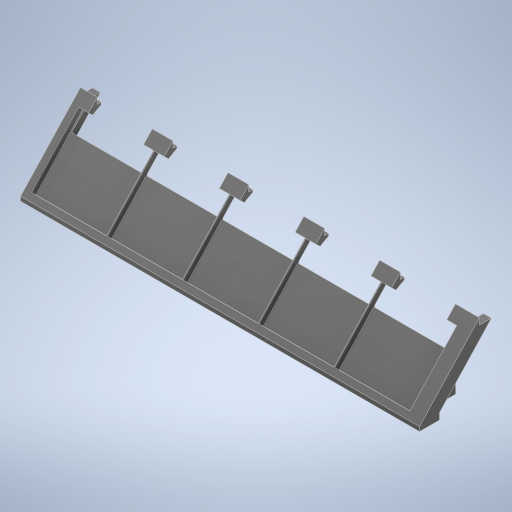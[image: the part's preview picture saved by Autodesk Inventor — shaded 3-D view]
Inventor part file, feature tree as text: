
AUTODESK INVENTOR PART (.ipt)
format: ipt  version: 2023 (Build 270158000, 158)  size: 503,808 bytes
history: native  units: mm
features: extrude x9, sketch x9, projected_geometry x8, plane x3, mirror x2, pattern_linear x1, chamfer x1
ambient origin geometry x8: Origin, YZ Plane, XZ Plane, XY Plane, X Axis, Y Axis, Z Axis, Center Point
bodies: Solid1 (feature_tree)
feature tree (33):
  extrude  "Extrusion1"  Depth=1.6mm
  plane  "Work Plane1"
  extrude  "Extrusion2"  Depth=4.0mm
  extrude  "Extrusion3"  Depth=3.0mm
  plane  "Work Plane2"
  mirror  "Mirror1"
  pattern_linear  "Rectangular Pattern1"  Count1=10 Spacing1=0.0mm
  extrude  "Extrusion4"  [1 undecoded]
  extrude  "Extrusion5"  Depth=3.0mm
  extrude  "Extrusion6"  Depth=3.0mm
  chamfer  "Chamfer1"  Distance=18.8mm
  extrude  "Extrusion7"  Depth=2.5mm TaperAngle=0.0deg
  extrude  "Extrusion8"  Depth=8.0mm
  plane  "Work Plane3"
  mirror  "Mirror2"
  extrude  "Extrusion9"  TaperAngle=0.0deg  [1 undecoded]
  sketch  "Sketch1"  dims[d0=1.6mm d1=1.970174mm]
  sketch  "Sketch2"  dims[d3=14.0mm d4=4.0mm]
  projected_geometry  "Projected Loop1"
  sketch  "Sketch3"  dims[d7=6.0mm d8=3.0mm]
  projected_geometry  "Projected Loop2"
  sketch  "Sketch5"  dims[d10=10.0mm d11=100.0mm d12=0.0mm]
  projected_geometry  "Projected Loop3"
  projected_geometry  "Projected Loop4"
  projected_geometry  "Projected Loop5"
  sketch  "Sketch6"  dims[d13=1.6mm d14=-3.5mm]
  sketch  "Sketch7"  dims[d15=1.5mm d16=3.0mm]
  projected_geometry  "Projected Loop6"
  sketch  "Sketch8"  dims[d17=1.0mm d18=3.0mm d19=18.8mm d20=0.0mm]
  projected_geometry  "Projected Loop7"
  sketch  "Sketch9"  dims[d21=17.3mm d22=2.5mm d23=0.0mm]
  projected_geometry  "Projected Loop8"
  sketch  "Sketch10"  dims[d24=50.0mm d26=19.0mm d27=8.0mm d28=0.0mm d29=0.0mm d30=0.8mm d31=1.0mm d32=10.0mm d33=0.0mm d34=0.0mm d35=0.0mm d36=0.31mm d37=2.0mm d38=45.0deg d39=2.0mm d40=0.0mm d41=2.0mm d42=0.0mm d43=1.0mm d44=0.0mm d45=0.0mm]
note: 2 required parameter values undecoded (feature->parameter linkage not recoverable at this tier; creation-order binding heuristic only, values carry confidence <= 0.55)
